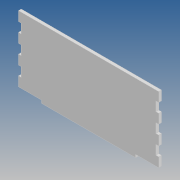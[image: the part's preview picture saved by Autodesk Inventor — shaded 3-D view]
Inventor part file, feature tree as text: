
AUTODESK INVENTOR PART (.ipt)
format: ipt  version: 2020 (Build 240168000, 168)  size: 122,368 bytes
history: native  units: mm
features: extrude x3, sketch x3, other x1, pattern_linear x1, mirror x1
ambient origin geometry x8: Origin, YZ Plane, XZ Plane, XY Plane, X Axis, Y Axis, Z Axis, Center Point
bodies: Body1 (feature_tree)
feature tree (9):
  other  "Твердое тело1"
  extrude  "Выдавливание1"  Depth=149.0mm
  extrude  "Выдавливание2"  Depth=70.0mm
  pattern_linear  "Прямоуг.массив1"  Spacing1=3.0mm  [1 undecoded]
  mirror  "Зеркальное отражение1"
  extrude  "Выдавливание3"  Depth=3.0mm
  sketch  "Эскиз1"
  sketch  "Эскиз2"
  sketch  "Эскиз3"
note: 1 required parameter value undecoded (feature->parameter linkage not recoverable at this tier; creation-order binding heuristic only, values carry confidence <= 0.55)
